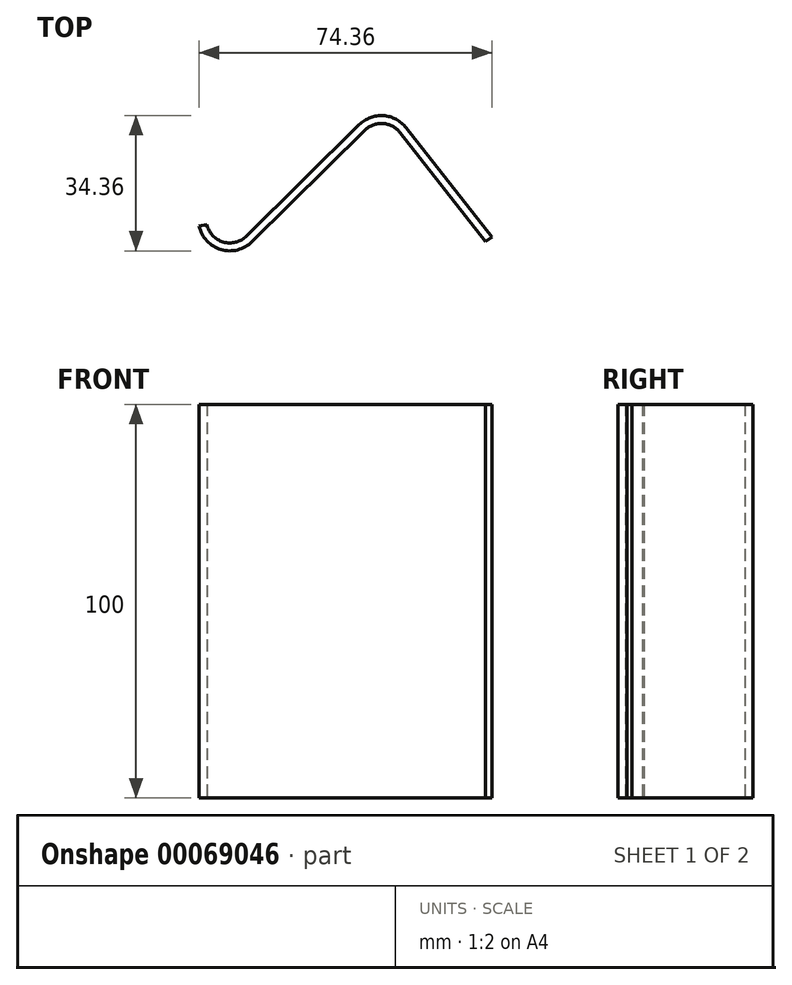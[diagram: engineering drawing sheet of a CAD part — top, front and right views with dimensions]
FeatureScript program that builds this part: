
annotation { "Feature Type Name" : "Feature", "Feature Type Description" : "" }
export const myFeature = defineFeature(function(context is Context, id is Id, definition is map)
    precondition{}
    {
        {
            var Q0;
            Q0=qCreatedBy(makeId("Top.planeOp"),FACE);
            var sketch = newSketch(context, id + "F0", { "sketchPlane" : qUnion([Q0])});
            skLineSegment(sketch, "E0", {"start": v(-33.42, 0) * mm, "end": v(-4.78, 28.31) * mm});
            skLineSegment(sketch, "E1", {"start": v(4.15, 27.75) * mm, "end": v(25.93, 0) * mm});
            skPoint(sketch, "E2.visualSharp", {"position": v(0, 33.04) * mm});
            skArc(sketch, "E2.filletArc", {"start": v(4.15, 27.75) * mm, "mid": v(-0.19, 30.03) * mm, "end": v(-4.78, 28.31) * mm});
            skArc(sketch, "E3", {"start": v(-33.42, 0) * mm, "mid": v(-41.3, -1.99) * mm, "end": v(-46.86, 3.95) * mm});
            skArc(sketch, "E4.0", {"start": v(-34.83, 1.42) * mm, "mid": v(-40.74, -0.07) * mm, "end": v(-44.9, 4.38) * mm});
            skLineSegment(sketch, "E4.1", {"start": v(-34.83, 1.42) * mm, "end": v(-6.2, 29.73) * mm});
            skArc(sketch, "E4.2", {"start": v(5.73, 28.98) * mm, "mid": v(-0.06, 32.03) * mm, "end": v(-6.2, 29.73) * mm});
            skLineSegment(sketch, "E4.3", {"start": v(5.73, 28.98) * mm, "end": v(27.5, 1.23) * mm});
            skLineSegment(sketch, "E5", {"start": v(-44.9, 4.38) * mm, "end": v(-46.86, 3.95) * mm});
            skLineSegment(sketch, "E6", {"start": v(27.5, 1.23) * mm, "end": v(25.93, 0) * mm});
            skSolve(sketch);
        }
        {
            var Q0;
            Q0=makeQuery(id+"F0.imprint","IMPRINT",FACE,{"disambiguationData":[TD([[makeQuery(id+"F0.imprint","IMPRINT",EDGE,{"derivedFrom":sQuery(id+"F0.wireOp",EDGE,"E0")}),1.0]])]});
            extrude(context, id + "F1", {"entities" : qUnion([Q0]), "depth" : 100 * mm});
        }
    });
